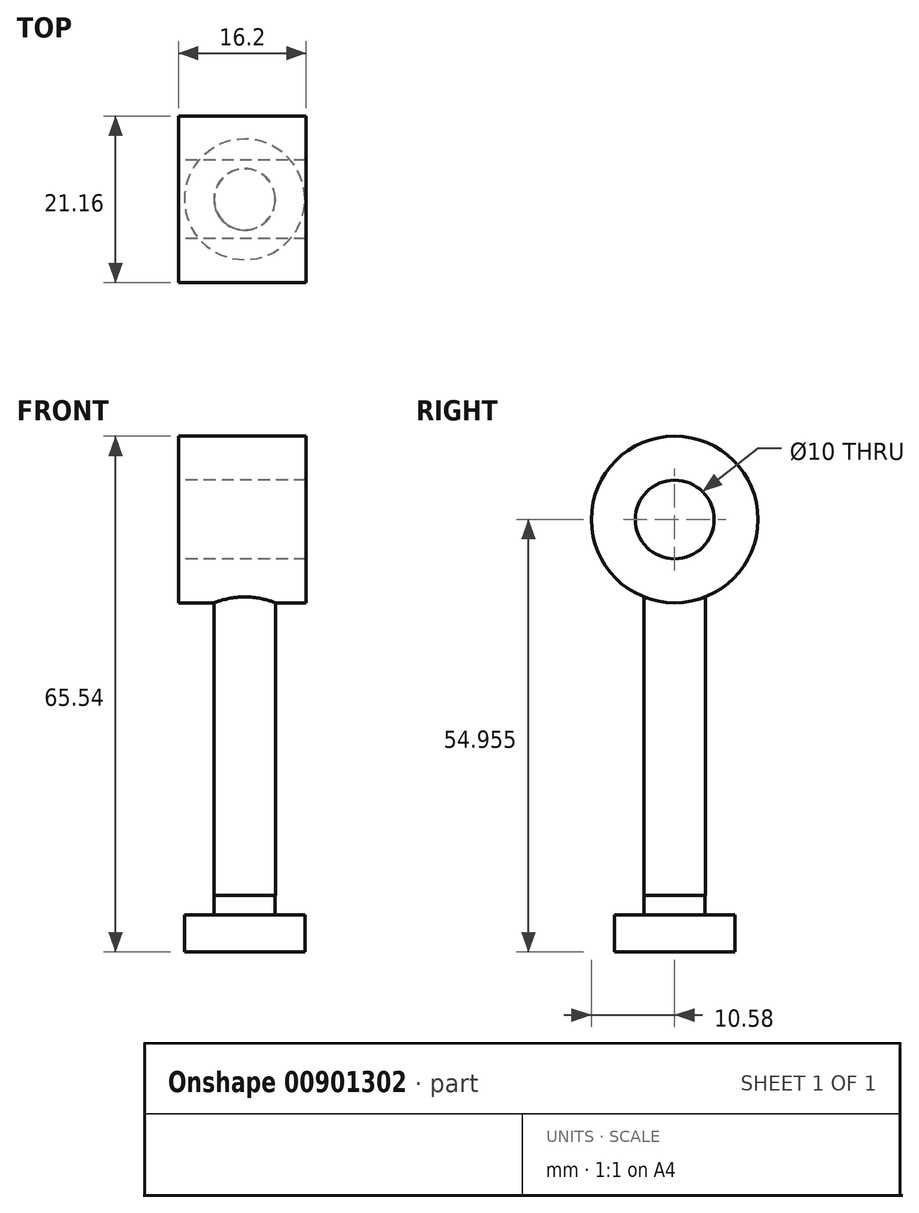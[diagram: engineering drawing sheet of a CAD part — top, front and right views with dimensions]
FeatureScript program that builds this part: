
annotation { "Feature Type Name" : "Feature", "Feature Type Description" : "" }
export const myFeature = defineFeature(function(context is Context, id is Id, definition is map)
    precondition{}
    {
        {
            var Q0;
            Q0=qCreatedBy(makeId("Front.planeOp"),FACE);
            var sketch = newSketch(context, id + "F0", { "sketchPlane" : qUnion([Q0])});
            skCircle(sketch, "E0", {"center": v(0, 8.26) * mm, "radius": 1.5 * mm});
            skSolve(sketch);
        }
        {
            var Q0;
            Q0 = qSketchRegion(id + "F0", true);
            extrude(context, id + "F1", {"entities" : qUnion([Q0]), "depth" : 20.2 * mm, "offsetDistance" : 25 * mm});
        }
        {
            var Q0;
            Q0=qCreatedBy(makeId("Front.planeOp"),FACE);
            var sketch = newSketch(context, id + "F2", { "sketchPlane" : qUnion([Q0])});
            skArc(sketch, "E1", {"start": v(0, 18.26) * mm, "mid": v(-10, 8.26) * mm, "end": v(0, -1.74) * mm});
            skLineSegment(sketch, "E2", {"start": v(0, 18.26) * mm, "end": v(0, -1.74) * mm});
            skSolve(sketch);
        }
        {
            var Q0;
            Q0 = qSketchRegion(id + "F2", true);
            var Q1;
            Q1=sQuery(id+"F2.wireOp",EDGE,"E2");
            revolve(context, id + "F3", {"operationType" : NewBodyOperationType.ADD, "surfaceOperationType" : NewSurfaceOperationType.NEW, "entities" : qUnion([Q0]), "axis" : qUnion([Q1]), "revolveType" : RevolveType.FULL});
        }
        {
            var Q0;
            Q0=qCreatedBy(makeId("Top.planeOp"),FACE);
            var sketch = newSketch(context, id + "F4", { "sketchPlane" : qUnion([Q0])});
            skCircle(sketch, "E3", {"center": v(0, 0) * mm, "radius": 4 * mm});
            skSolve(sketch);
        }
        {
            var Q0;
            Q0 = qSketchRegion(id + "F4", true);
            extrude(context, id + "F5", {"entities" : qUnion([Q0]), "operationType" : NewBodyOperationType.REMOVE, "depth" : 45.1 * mm, "offsetDistance" : 25 * mm});
        }
        {
            var Q0;
            Q0=qCreatedBy(makeId("Top.planeOp"),FACE);
            var sketch = newSketch(context, id + "F6", { "sketchPlane" : qUnion([Q0])});
            skCircle(sketch, "E4", {"center": v(0, 0) * mm, "radius": 3 * mm});
            skSolve(sketch);
        }
        {
            var Q0;
            Q0 = qSketchRegion(id + "F6", true);
            extrude(context, id + "F7", {"entities" : qUnion([Q0]), "operationType" : NewBodyOperationType.ADD, "oppositeDirection" : true, "depth" : 30.3 * mm, "offsetDistance" : 25 * mm});
        }
        {
            var Q0;
            Q0 = qSketchRegion(id + "F4", true);
            extrude(context, id + "F8", {"entities" : qUnion([Q0]), "operationType" : NewBodyOperationType.REMOVE, "oppositeDirection" : true, "depth" : 25 * mm, "offsetDistance" : 25 * mm});
        }
        {
            var Q0;
            Q0=qCreatedBy(makeId("Top.planeOp"),FACE);
            var sketch = newSketch(context, id + "F9", { "sketchPlane" : qUnion([Q0])});
            skCircle(sketch, "E5", {"center": v(0, 0) * mm, "radius": 3.95 * mm});
            skSolve(sketch);
        }
        {
            var Q0;
            Q0 = qSketchRegion(id + "F9", true);
            extrude(context, id + "F10", {"entities" : qUnion([Q0]), "operationType" : NewBodyOperationType.ADD, "oppositeDirection" : true, "depth" : 66.9 * mm, "offsetDistance" : 25 * mm});
        }
        {
            var Q0;
            Q0=makeQuery(id+"F8.boolean.opBoolean","SPLIT",BODY,{"disambiguationData":[OD(1.0)],"derivedFrom":makeQuery(id+"F1.opExtrude","SWEPT_BODY",BODY,{"disambiguationData":[OSD([sQuery(id+"F0.wireOp",EDGE,"E0")])]})});
            deleteBodies(context, id + "F11", {"entities" : qUnion([Q0])});
        }
        {
            var Q0;
            Q0=qCreatedBy(makeId("Top.planeOp"),FACE);
            var sketch = newSketch(context, id + "F12", { "sketchPlane" : qUnion([Q0])});
            skCircle(sketch, "E6", {"center": v(0, 0) * mm, "radius": 3.9 * mm});
            skSolve(sketch);
        }
        {
            var Q0;
            Q0 = qSketchRegion(id + "F12", true);
            extrude(context, id + "F13", {"entities" : qUnion([Q0]), "depth" : 48 * mm, "offsetDistance" : 25 * mm});
        }
        {
            var Q0;
            Q0=qCreatedBy(makeId("Top.planeOp"),FACE);
            cPlane(context, id + "F14", {"entities" : qUnion([Q0]), "cplaneType" : CPlaneType.OFFSET, "offset" : 25 * mm, "width" : 150 * mm, "height" : 150 * mm});
        }
        {
            var Q0;
            Q0=qCreatedBy(id+"F14.planeOp",FACE);
            var sketch = newSketch(context, id + "F15", { "sketchPlane" : qUnion([Q0])});
            skCircle(sketch, "E7", {"center": v(0, 0) * mm, "radius": 3.88 * mm});
            skSolve(sketch);
        }
        {
            var Q0;
            Q0 = qSketchRegion(id + "F15", true);
            extrude(context, id + "F16", {"entities" : qUnion([Q0]), "operationType" : NewBodyOperationType.ADD, "oppositeDirection" : true, "depth" : 32 * mm, "offsetDistance" : 25 * mm});
        }
        {
            var Q0;
            Q0=qCreatedBy(makeId("Top.planeOp"),FACE);
            cPlane(context, id + "F17", {"entities" : qUnion([Q0]), "cplaneType" : CPlaneType.OFFSET, "offset" : 2.5 * mm, "oppositeDirection" : true, "width" : 150 * mm, "height" : 150 * mm});
        }
        {
            var Q0;
            Q0=qCreatedBy(id+"F17.planeOp",FACE);
            var sketch = newSketch(context, id + "F18", { "sketchPlane" : qUnion([Q0])});
            skCircle(sketch, "E8", {"center": v(0, 0) * mm, "radius": 7.65 * mm});
            skSolve(sketch);
        }
        {
            var Q0;
            Q0 = qSketchRegion(id + "F18", true);
            extrude(context, id + "F19", {"entities" : qUnion([Q0]), "operationType" : NewBodyOperationType.ADD, "oppositeDirection" : true, "depth" : 4.7 * mm, "offsetDistance" : 25 * mm});
        }
        {
            var Q0;
            Q0=qCreatedBy(makeId("Right.planeOp"),FACE);
            var sketch = newSketch(context, id + "F20", { "sketchPlane" : qUnion([Q0])});
            skCircle(sketch, "E9", {"center": v(0, 47.75) * mm, "radius": 10.58 * mm});
            skSolve(sketch);
        }
        {
            var Q0;
            Q0 = qSketchRegion(id + "F20", true);
            extrude(context, id + "F21", {"entities" : qUnion([Q0]), "operationType" : NewBodyOperationType.ADD, "depth" : 7.8 * mm, "offsetDistance" : 25 * mm});
        }
        {
            var Q0;
            Q0=makeQuery(id+"F21.opExtrude","CAP_FACE",FACE,{"disambiguationData":[OSD([sQuery(id+"F20.wireOp",EDGE,"E9")])],"isStart":false});
            extrude(context, id + "F22", {"entities" : qUnion([Q0]), "operationType" : NewBodyOperationType.ADD, "oppositeDirection" : true, "depth" : 16.2 * mm, "offsetDistance" : 25 * mm});
        }
        {
            var Q0;
            Q0=makeQuery(id+"F22.opExtrude","CAP_FACE",FACE,{"disambiguationData":[OSD([sQuery(id+"F20.wireOp",EDGE,"E9")])],"isStart":false});
            var sketch = newSketch(context, id + "F23", { "sketchPlane" : qUnion([Q0])});
            skCircle(sketch, "E10", {"center": v(0, 47.75) * mm, "radius": 5 * mm});
            skSolve(sketch);
        }
        {
            var Q0;
            Q0 = qSketchRegion(id + "F23", true);
            extrude(context, id + "F24", {"entities" : qUnion([Q0]), "operationType" : NewBodyOperationType.REMOVE, "oppositeDirection" : true, "depth" : 25 * mm, "offsetDistance" : 25 * mm});
        }
    });
